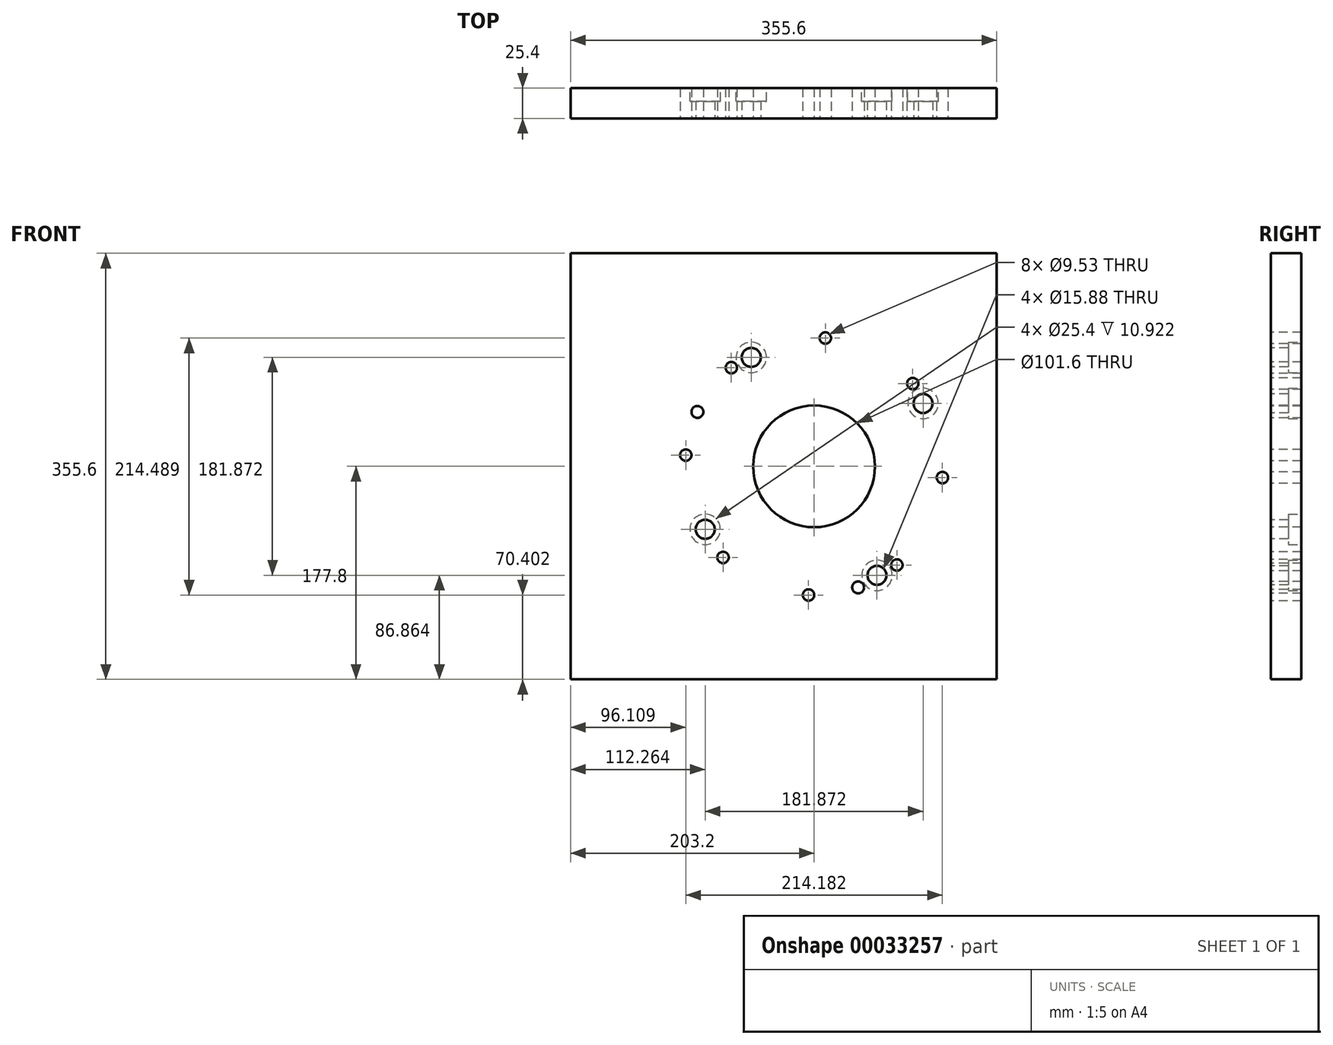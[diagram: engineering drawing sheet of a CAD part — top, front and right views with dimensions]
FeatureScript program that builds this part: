
annotation { "Feature Type Name" : "Feature", "Feature Type Description" : "" }
export const myFeature = defineFeature(function(context is Context, id is Id, definition is map)
    precondition{}
    {
        {
            var Q0;
            Q0=qCreatedBy(makeId("Front.planeOp"),FACE);
            var sketch = newSketch(context, id + "F0", { "sketchPlane" : qUnion([Q0])});
            skLineSegment(sketch, "E0.bottom", {"start": v(0, 0) * mm, "end": v(-355.6, 0) * mm});
            skLineSegment(sketch, "E0.top", {"start": v(0, 355.6) * mm, "end": v(-355.6, 355.6) * mm});
            skLineSegment(sketch, "E0.left", {"start": v(0, 0) * mm, "end": v(0, 355.6) * mm});
            skLineSegment(sketch, "E0.right", {"start": v(-355.6, 0) * mm, "end": v(-355.6, 355.6) * mm});
            skSolve(sketch);
        }
        {
            var Q0;
            Q0 = qSketchRegion(id + "F0", true);
            extrude(context, id + "F1", {"entities" : qUnion([Q0]), "depth" : 25.4 * mm});
        }
        {
            var Q0;
            Q0=makeQuery(id+"F1.opExtrude","CAP_FACE",FACE,{"disambiguationData":[OSD([sQuery(id+"F0.wireOp",EDGE,"E0.bottom"),sQuery(id+"F0.wireOp",EDGE,"E0.top"),sQuery(id+"F0.wireOp",EDGE,"E0.left"),sQuery(id+"F0.wireOp",EDGE,"E0.right")])],"isStart":false});
            var sketch = newSketch(context, id + "F2", { "sketchPlane" : qUnion([Q0])});
            skLineSegment(sketch, "E1", {"start": v(-152.4, 355.6) * mm, "end": v(-152.4, 177.8) * mm, "construction": true});
            skLineSegment(sketch, "E2", {"start": v(-152.4, 177.8) * mm, "end": v(-355.6, 177.8) * mm, "construction": true});
            skCircle(sketch, "E3", {"center": v(-152.4, 177.8) * mm, "radius": 107.5 * mm, "construction": true});
            skLineSegment(sketch, "E4", {"start": v(-152.4, 177.8) * mm, "end": v(-259.5, 187.17) * mm, "construction": true});
            skLineSegment(sketch, "E5", {"start": v(-152.4, 177.8) * mm, "end": v(-45.3, 168.43) * mm, "construction": true});
            skLineSegment(sketch, "E6", {"start": v(-152.4, 177.8) * mm, "end": v(-249.83, 223.23) * mm, "construction": true});
            skLineSegment(sketch, "E7", {"start": v(-152.4, 177.8) * mm, "end": v(-221.5, 260.15) * mm, "construction": true});
            skLineSegment(sketch, "E8", {"start": v(-152.4, 177.8) * mm, "end": v(-143.03, 284.9) * mm, "construction": true});
            skLineSegment(sketch, "E9", {"start": v(-152.4, 177.8) * mm, "end": v(-70.05, 246.9) * mm, "construction": true});
            skLineSegment(sketch, "E10", {"start": v(-152.4, 177.8) * mm, "end": v(-83.3, 95.45) * mm, "construction": true});
            skLineSegment(sketch, "E11", {"start": v(-152.4, 177.8) * mm, "end": v(-115.63, 76.78) * mm, "construction": true});
            skLineSegment(sketch, "E12", {"start": v(-152.4, 177.8) * mm, "end": v(-157.09, 70.4) * mm, "construction": true});
            skLineSegment(sketch, "E13", {"start": v(-152.4, 177.8) * mm, "end": v(-228.41, 101.79) * mm, "construction": true});
            skCircle(sketch, "E14", {"center": v(-259.5, 187.17) * mm, "radius": 4.76 * mm});
            skCircle(sketch, "E15", {"center": v(-221.5, 260.15) * mm, "radius": 4.76 * mm});
            skCircle(sketch, "E16", {"center": v(-143.03, 284.9) * mm, "radius": 4.76 * mm});
            skCircle(sketch, "E17", {"center": v(-70.05, 246.9) * mm, "radius": 4.76 * mm});
            skCircle(sketch, "E18", {"center": v(-45.3, 168.43) * mm, "radius": 4.76 * mm});
            skCircle(sketch, "E19", {"center": v(-83.3, 95.45) * mm, "radius": 4.76 * mm});
            skCircle(sketch, "E20", {"center": v(-157.09, 70.4) * mm, "radius": 4.76 * mm});
            skCircle(sketch, "E21", {"center": v(-228.41, 101.79) * mm, "radius": 4.76 * mm});
            skCircle(sketch, "E22", {"center": v(-249.83, 223.23) * mm, "radius": 4.98 * mm});
            skCircle(sketch, "E23", {"center": v(-115.63, 76.78) * mm, "radius": 4.98 * mm});
            skCircle(sketch, "E24", {"center": v(-152.4, 177.8) * mm, "radius": 50.8 * mm});
            skSolve(sketch);
        }
        {
            var Q0;
            Q0 = qSketchRegion(id + "F2", true);
            extrude(context, id + "F3", {"entities" : qUnion([Q0]), "operationType" : NewBodyOperationType.REMOVE, "endBound" : BoundingType.THROUGH_ALL, "oppositeDirection" : true, "depth" : 25.4 * mm});
        }
        {
            var Q0;
            Q0=makeQuery(id+"F1.opExtrude","CAP_FACE",FACE,{"disambiguationData":[OSD([sQuery(id+"F0.wireOp",EDGE,"E0.bottom"),sQuery(id+"F0.wireOp",EDGE,"E0.top"),sQuery(id+"F0.wireOp",EDGE,"E0.left"),sQuery(id+"F0.wireOp",EDGE,"E0.right")])],"isStart":false});
            var sketch = newSketch(context, id + "F4", { "sketchPlane" : qUnion([Q0])});
            skCircle(sketch, "E25", {"center": v(-152.4, 177.8) * mm, "radius": 105 * mm, "construction": true});
            skLineSegment(sketch, "E26", {"start": v(-152.4, 177.8) * mm, "end": v(-47.4, 177.8) * mm});
            skLineSegment(sketch, "E27", {"start": v(-152.4, 177.8) * mm, "end": v(-61.46, 230.3) * mm, "construction": true});
            skLineSegment(sketch, "E28", {"start": v(-152.4, 177.8) * mm, "end": v(-204.9, 268.74) * mm, "construction": true});
            skLineSegment(sketch, "E29", {"start": v(-152.4, 177.8) * mm, "end": v(-243.34, 125.3) * mm, "construction": true});
            skLineSegment(sketch, "E30", {"start": v(-152.4, 177.8) * mm, "end": v(-99.9, 86.86) * mm, "construction": true});
            skCircle(sketch, "E31", {"center": v(-204.9, 268.74) * mm, "radius": 7.94 * mm});
            skCircle(sketch, "E32", {"center": v(-243.34, 125.3) * mm, "radius": 7.94 * mm});
            skCircle(sketch, "E33", {"center": v(-99.9, 86.86) * mm, "radius": 7.94 * mm});
            skCircle(sketch, "E34", {"center": v(-61.46, 230.3) * mm, "radius": 7.94 * mm});
            skSolve(sketch);
        }
        {
            var Q0;
            Q0 = qSketchRegion(id + "F4", true);
            extrude(context, id + "F5", {"entities" : qUnion([Q0]), "operationType" : NewBodyOperationType.REMOVE, "endBound" : BoundingType.THROUGH_ALL, "oppositeDirection" : true, "depth" : 25.4 * mm});
        }
        {
            var Q0;
            Q0=makeQuery(id+"F1.opExtrude","CAP_FACE",FACE,{"disambiguationData":[OSD([sQuery(id+"F0.wireOp",EDGE,"E0.bottom"),sQuery(id+"F0.wireOp",EDGE,"E0.top"),sQuery(id+"F0.wireOp",EDGE,"E0.left"),sQuery(id+"F0.wireOp",EDGE,"E0.right")])],"isStart":true});
            var sketch = newSketch(context, id + "F6", { "sketchPlane" : qUnion([Q0])});
            skCircle(sketch, "E35", {"center": v(204.9, 268.74) * mm, "radius": 12.7 * mm});
            skCircle(sketch, "E36", {"center": v(243.34, 125.3) * mm, "radius": 12.7 * mm});
            skCircle(sketch, "E37", {"center": v(99.9, 86.86) * mm, "radius": 12.7 * mm});
            skCircle(sketch, "E38", {"center": v(61.46, 230.3) * mm, "radius": 12.7 * mm});
            skSolve(sketch);
        }
        {
            var Q0;
            Q0 = qSketchRegion(id + "F6", true);
            extrude(context, id + "F7", {"entities" : qUnion([Q0]), "operationType" : NewBodyOperationType.REMOVE, "oppositeDirection" : true, "depth" : 10.92 * mm});
        }
    });
